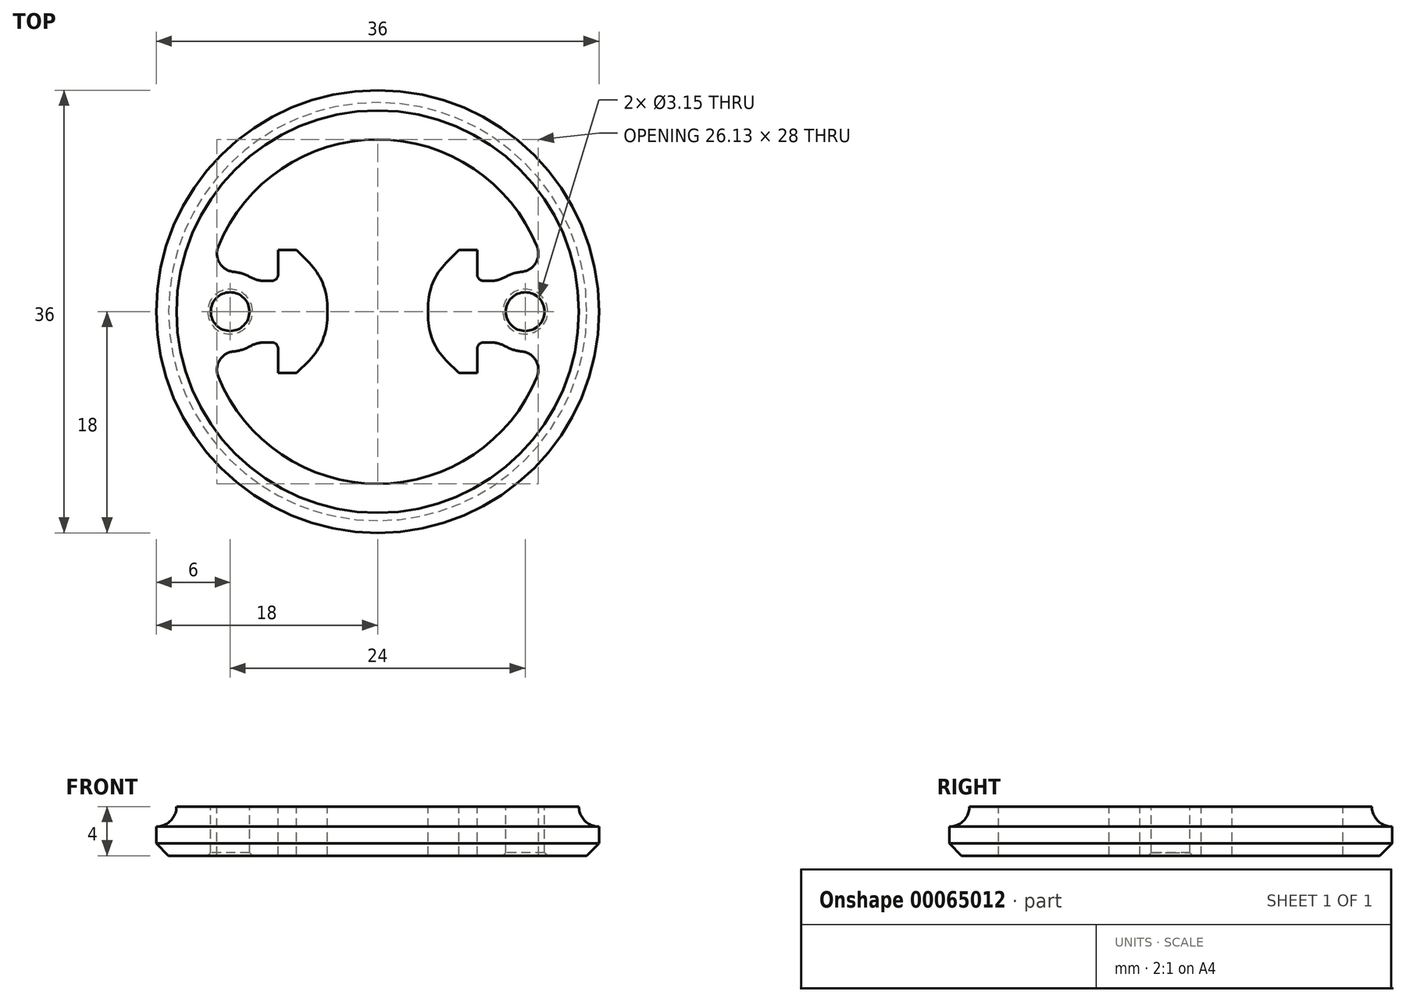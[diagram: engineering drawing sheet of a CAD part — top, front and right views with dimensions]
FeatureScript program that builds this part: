
annotation { "Feature Type Name" : "Feature", "Feature Type Description" : "" }
export const myFeature = defineFeature(function(context is Context, id is Id, definition is map)
    precondition{}
    {
        {
            var Q0;
            Q0=qCreatedBy(makeId("Right.planeOp"),FACE);
            var sketch = newSketch(context, id + "F0", { "sketchPlane" : qUnion([Q0])});
            skLineSegment(sketch, "E0", {"start": v(0, 0) * mm, "end": v(0, -1.49) * mm, "construction": true});
            skLineSegment(sketch, "E1", {"start": v(14, 0) * mm, "end": v(14, -4) * mm});
            skLineSegment(sketch, "E2", {"start": v(14, -4) * mm, "end": v(18, -4) * mm});
            skLineSegment(sketch, "E3", {"start": v(18, -4) * mm, "end": v(18, -1.64) * mm});
            skLineSegment(sketch, "E4", {"start": v(14, 0) * mm, "end": v(16.36, 0) * mm});
            skArc(sketch, "E5", {"start": v(16.36, 0) * mm, "mid": v(16.84, -1.16) * mm, "end": v(18, -1.64) * mm});
            skSolve(sketch);
        }
        {
            var Q0;
            Q0=makeQuery(id+"F0.imprint","IMPRINT",FACE,{"disambiguationData":[TD([[makeQuery(id+"F0.imprint","IMPRINT",EDGE,{"derivedFrom":sQuery(id+"F0.wireOp",EDGE,"E1")}),1.0]])]});
            var Q1;
            Q1=sQuery(id+"F0.wireOp",EDGE,"E0");
            revolve(context, id + "F1", {"entities" : qUnion([Q0]), "axis" : qUnion([Q1]), "revolveType" : RevolveType.FULL});
        }
        {
            var Q0;
            Q0=makeQuery(id+"F1.opRevolve","SWEPT_FACE",FACE,{"disambiguationData":[OSD([sQuery(id+"F0.wireOp",EDGE,"E4")])]});
            var sketch = newSketch(context, id + "F2", { "sketchPlane" : qUnion([Q0])});
            skCircle(sketch, "E6.0", {"center": v(0, 0) * mm, "radius": 14 * mm, "construction": true});
            skCircle(sketch, "E7", {"center": v(-12, 0) * mm, "radius": 1.57 * mm});
            skArc(sketch, "E8", {"start": v(-9.92, 2.5) * mm, "mid": v(-10.76, 3) * mm, "end": v(-11.7, 3.24) * mm});
            skLineSegment(sketch, "E9", {"start": v(-9.92, -2.5) * mm, "end": v(-8.1, -2.5) * mm});
            skLineSegment(sketch, "E10", {"start": v(-9.92, 2.5) * mm, "end": v(-8.1, 2.5) * mm});
            skLineSegment(sketch, "E11", {"start": v(-8.1, 2.5) * mm, "end": v(-8.1, 5) * mm});
            skLineSegment(sketch, "E12", {"start": v(-4.1, 2.5) * mm, "end": v(-4.1, -2.5) * mm});
            skLineSegment(sketch, "E13", {"start": v(-8.1, -5) * mm, "end": v(-8.1, -2.5) * mm});
            skCircle(sketch, "E14.0", {"center": v(0, 0) * mm, "radius": 16.36 * mm, "construction": true});
            skLineSegment(sketch, "E15", {"start": v(-4.1, 0) * mm, "end": v(-12, 0) * mm, "construction": true});
            skLineSegment(sketch, "E16", {"start": v(-8.1, -5) * mm, "end": v(-6.6, -5) * mm});
            skLineSegment(sketch, "E17", {"start": v(-6.6, -5) * mm, "end": v(-4.1, -2.5) * mm});
            skLineSegment(sketch, "E18", {"start": v(-8.1, 5) * mm, "end": v(-6.6, 5) * mm});
            skLineSegment(sketch, "E19", {"start": v(-6.6, 5) * mm, "end": v(-4.1, 2.5) * mm});
            skArc(sketch, "E20", {"start": v(-12.96, 5.3) * mm, "mid": v(-14, 0) * mm, "end": v(-12.96, -5.3) * mm});
            skArc(sketch, "E21", {"start": v(-11.7, -3.24) * mm, "mid": v(-12.85, -3.95) * mm, "end": v(-12.96, -5.3) * mm});
            skArc(sketch, "E22", {"start": v(-12.96, 5.3) * mm, "mid": v(-12.85, 3.95) * mm, "end": v(-11.7, 3.24) * mm});
            skArc(sketch, "E23.trimOffspring", {"start": v(-11.7, -3.24) * mm, "mid": v(-10.76, -3) * mm, "end": v(-9.92, -2.5) * mm});
            skSolve(sketch);
        }
        {
            var Q0;
            {var subQ5=sQuery(id+"F2.wireOp",EDGE,"E9");Q0=makeQuery(id+"F2.imprint","IMPRINT",FACE,{"disambiguationData":[TD([[makeQuery(id+"F2.imprint","IMPRINT",EDGE,{"derivedFrom":subQ5}),1.0]])]});}
            var Q1;
            Q1=makeQuery(id+"F1.opRevolve","SWEPT_FACE",FACE,{"disambiguationData":[OSD([sQuery(id+"F0.wireOp",EDGE,"E2")])]});
            extrude(context, id + "F3", {"entities" : qUnion([Q0]), "operationType" : NewBodyOperationType.ADD, "endBound" : BoundingType.UP_TO_SURFACE, "oppositeDirection" : true, "endBoundEntityFace" : qUnion([Q1]), "depth" : 25 * mm});
        }
        {
            var Q0;
            Q0=makeQuery(id+"F1.opRevolve","SWEPT_BODY",BODY,{"disambiguationData":[OSD([sQuery(id+"F0.wireOp",EDGE,"E1"),sQuery(id+"F0.wireOp",EDGE,"5vlPOog4-GuGJ-TXkg-PQnt-qaFtN5Dd3R6W"),sQuery(id+"F0.wireOp",EDGE,"CSWl2GdR-jlEp-lZkL-Fedu-TW51tIPRqq1U"),sQuery(id+"F0.wireOp",EDGE,"E2"),sQuery(id+"F0.wireOp",EDGE,"E3"),sQuery(id+"F0.wireOp",EDGE,"E4"),sQuery(id+"F0.wireOp",EDGE,"E5"),sQuery(id+"F0.wireOp",EDGE,"ccb59742-3ff2-4592-bd28-642af8389996.filletArc")])]});
            var Q1;
            {var subQ0=sQuery(id+"F2.wireOp",EDGE,"E8");Q1=makeQuery(id+"F3.opExtrude","SWEPT_FACE",FACE,{"disambiguationData":[OSD([subQ0]),TDD([makeQuery(id+"F2.imprint","IMPRINT",EDGE,{"disambiguationData":[TD([[makeQuery(id+"F2.imprint","INTERSECT",VERTEX,{"derivedFrom":[subQ0,sQuery(id+"F2.wireOp",EDGE,"E9")]}),1.0]])],"derivedFrom":subQ0})])]});}
            var Q2;
            Q2=makeQuery(id+"F3.opExtrude","SWEPT_FACE",FACE,{"disambiguationData":[OSD([sQuery(id+"F2.wireOp",EDGE,"E9")])]});
            var Q3;
            Q3=makeQuery(id+"F3.opExtrude","SWEPT_FACE",FACE,{"disambiguationData":[OSD([sQuery(id+"F2.wireOp",EDGE,"E13")])]});
            var Q4;
            Q4=makeQuery(id+"F3.opExtrude","SWEPT_FACE",FACE,{"disambiguationData":[OSD([sQuery(id+"F2.wireOp",EDGE,"E16")])]});
            var Q5;
            Q5=makeQuery(id+"F3.opExtrude","SWEPT_FACE",FACE,{"disambiguationData":[OSD([sQuery(id+"F2.wireOp",EDGE,"E17")])]});
            var Q6;
            Q6=makeQuery(id+"F3.opExtrude","SWEPT_FACE",FACE,{"disambiguationData":[OSD([sQuery(id+"F2.wireOp",EDGE,"E12")])]});
            var Q7;
            Q7=makeQuery(id+"F3.opExtrude","SWEPT_FACE",FACE,{"disambiguationData":[OSD([sQuery(id+"F2.wireOp",EDGE,"E19")])]});
            var Q8;
            Q8=makeQuery(id+"F3.opExtrude","SWEPT_FACE",FACE,{"disambiguationData":[OSD([sQuery(id+"F2.wireOp",EDGE,"E18")])]});
            var Q9;
            Q9=makeQuery(id+"F3.opExtrude","SWEPT_FACE",FACE,{"disambiguationData":[OSD([sQuery(id+"F2.wireOp",EDGE,"E10")])]});
            var Q10;
            {var subQ0=sQuery(id+"F2.wireOp",EDGE,"E8");Q10=makeQuery(id+"F3.opExtrude","SWEPT_FACE",FACE,{"disambiguationData":[OSD([subQ0]),TDD([makeQuery(id+"F2.imprint","IMPRINT",EDGE,{"disambiguationData":[TD([[makeQuery(id+"F2.imprint","INTERSECT",VERTEX,{"derivedFrom":[subQ0,sQuery(id+"F2.wireOp",EDGE,"E10")]}),-1.0]])],"derivedFrom":subQ0})])]});}
            var Q11;
            Q11=makeQuery(id+"F3.opExtrude","SWEPT_FACE",FACE,{"disambiguationData":[OSD([sQuery(id+"F2.wireOp",EDGE,"E11")])]});
            var Q12;
            Q12=makeQuery(id+"F3.opExtrude","SWEPT_FACE",FACE,{"disambiguationData":[OSD([sQuery(id+"F2.wireOp",EDGE,"E7")])]});
            var Q13;
            {var subQ8=sQuery(id+"F2.wireOp",EDGE,"E10");var subQ10=sQuery(id+"F2.wireOp",EDGE,"E8");var subQ12=sQuery(id+"F0.wireOp",EDGE,"E1");Q13=makeQuery(id+"F3.boolean.opBoolean","SPLIT",FACE,{"disambiguationData":[TD([makeQuery(id+"F3.opExtrude","SWEPT_FACE",FACE,{"disambiguationData":[OSD([subQ10]),TDD([makeQuery(id+"F2.imprint","IMPRINT",EDGE,{"disambiguationData":[TD([[makeQuery(id+"F2.imprint","INTERSECT",VERTEX,{"derivedFrom":[subQ10,subQ8]}),-1.0]])],"derivedFrom":subQ10})])]})])],"derivedFrom":makeQuery(id+"F1.opRevolve","SWEPT_FACE",FACE,{"disambiguationData":[OSD([subQ12])]})});}
            circularPattern(context, id + "F4", {"operationType" : NewBodyOperationType.ADD, "entities" : qUnion([Q0]), "axis" : qUnion([Q13]), "angle" : 360 * degree, "instanceCount" : 2, "equalSpace" : true});
        }
        {
            var Q0;
            Q0=makeQuery(id+"F3.opExtrude","SWEPT_EDGE",EDGE,{"disambiguationData":[OSD([sQuery(id+"F2.wireOp",EDGE,"E12"),sQuery(id+"F2.wireOp",EDGE,"E17")])]});
            var Q1;
            Q1=makeQuery(id+"F3.opExtrude","SWEPT_EDGE",EDGE,{"disambiguationData":[OSD([sQuery(id+"F2.wireOp",EDGE,"E12"),sQuery(id+"F2.wireOp",EDGE,"E19")])]});
            var Q2;
            Q2=makeQuery(id+"F4.opPattern","COPY",EDGE,{"derivedFrom":makeQuery(id+"F3.opExtrude","SWEPT_EDGE",EDGE,{"disambiguationData":[OSD([sQuery(id+"F2.wireOp",EDGE,"E12"),sQuery(id+"F2.wireOp",EDGE,"E17")])]}),"instanceName":"1"});
            var Q3;
            Q3=makeQuery(id+"F4.opPattern","COPY",EDGE,{"derivedFrom":makeQuery(id+"F3.opExtrude","SWEPT_EDGE",EDGE,{"disambiguationData":[OSD([sQuery(id+"F2.wireOp",EDGE,"E12"),sQuery(id+"F2.wireOp",EDGE,"E19")])]}),"instanceName":"1"});
            fillet(context, id + "F5", {"entities" : qUnion([Q0, Q1, Q2, Q3]), "radius" : 5 * mm, "tangentPropagation" : true, "allowEdgeOverflow" : false});
        }
        {
            var Q0;
            Q0=makeQuery(id+"F3.opExtrude","SWEPT_EDGE",EDGE,{"disambiguationData":[OSD([sQuery(id+"F2.wireOp",EDGE,"E8"),sQuery(id+"F2.wireOp",EDGE,"E10")])]});
            var Q1;
            Q1=makeQuery(id+"F3.opExtrude","SWEPT_EDGE",EDGE,{"disambiguationData":[OSD([sQuery(id+"F2.wireOp",EDGE,"E9"),sQuery(id+"F2.wireOp",EDGE,"E23.trimOffspring")])]});
            var Q2;
            Q2=makeQuery(id+"F4.opPattern","COPY",EDGE,{"derivedFrom":makeQuery(id+"F3.opExtrude","SWEPT_EDGE",EDGE,{"disambiguationData":[OSD([sQuery(id+"F2.wireOp",EDGE,"E9"),sQuery(id+"F2.wireOp",EDGE,"E23.trimOffspring")])]}),"instanceName":"1"});
            var Q3;
            Q3=makeQuery(id+"F4.opPattern","COPY",EDGE,{"derivedFrom":makeQuery(id+"F3.opExtrude","SWEPT_EDGE",EDGE,{"disambiguationData":[OSD([sQuery(id+"F2.wireOp",EDGE,"E8"),sQuery(id+"F2.wireOp",EDGE,"E10")])]}),"instanceName":"1"});
            fillet(context, id + "F6", {"entities" : qUnion([Q0, Q1, Q2, Q3]), "radius" : 2.5 * mm, "tangentPropagation" : true, "allowEdgeOverflow" : false});
        }
        {
            var Q0;
            Q0=makeQuery(id+"F3.opExtrude","SWEPT_EDGE",EDGE,{"disambiguationData":[OSD([sQuery(id+"F2.wireOp",EDGE,"E10"),sQuery(id+"F2.wireOp",EDGE,"E11")])]});
            var Q1;
            Q1=makeQuery(id+"F3.opExtrude","SWEPT_EDGE",EDGE,{"disambiguationData":[OSD([sQuery(id+"F2.wireOp",EDGE,"E9"),sQuery(id+"F2.wireOp",EDGE,"E13")])]});
            var Q2;
            Q2=makeQuery(id+"F4.opPattern","COPY",EDGE,{"derivedFrom":makeQuery(id+"F3.opExtrude","SWEPT_EDGE",EDGE,{"disambiguationData":[OSD([sQuery(id+"F2.wireOp",EDGE,"E10"),sQuery(id+"F2.wireOp",EDGE,"E11")])]}),"instanceName":"1"});
            var Q3;
            Q3=makeQuery(id+"F4.opPattern","COPY",EDGE,{"derivedFrom":makeQuery(id+"F3.opExtrude","SWEPT_EDGE",EDGE,{"disambiguationData":[OSD([sQuery(id+"F2.wireOp",EDGE,"E9"),sQuery(id+"F2.wireOp",EDGE,"E13")])]}),"instanceName":"1"});
            fillet(context, id + "F7", {"entities" : qUnion([Q0, Q1, Q2, Q3]), "radius" : 0.5 * mm, "tangentPropagation" : true, "allowEdgeOverflow" : false});
        }
        {
            var Q0;
            Q0=makeQuery(id+"F1.opRevolve","SWEPT_EDGE",EDGE,{"disambiguationData":[OSD([sQuery(id+"F0.wireOp",EDGE,"E2"),sQuery(id+"F0.wireOp",EDGE,"E3")])]});
            chamfer(context, id + "F8", {"entities" : qUnion([Q0]), "width" : 1 * mm, "tangentPropagation" : true});
        }
        {
            var Q0;
            Q0=makeQuery(id+"F4.opPattern","COPY",EDGE,{"derivedFrom":makeQuery(id+"F3.opExtrude","CAP_EDGE",EDGE,{"disambiguationData":[OSD([sQuery(id+"F2.wireOp",EDGE,"E7")])],"isStart":false}),"instanceName":"1"});
            var Q1;
            Q1=makeQuery(id+"F3.opExtrude","CAP_EDGE",EDGE,{"disambiguationData":[OSD([sQuery(id+"F2.wireOp",EDGE,"E7")])],"isStart":false});
            chamfer(context, id + "F9", {"entities" : qUnion([Q0, Q1]), "width" : 0.25 * mm, "tangentPropagation" : true});
        }
    });
